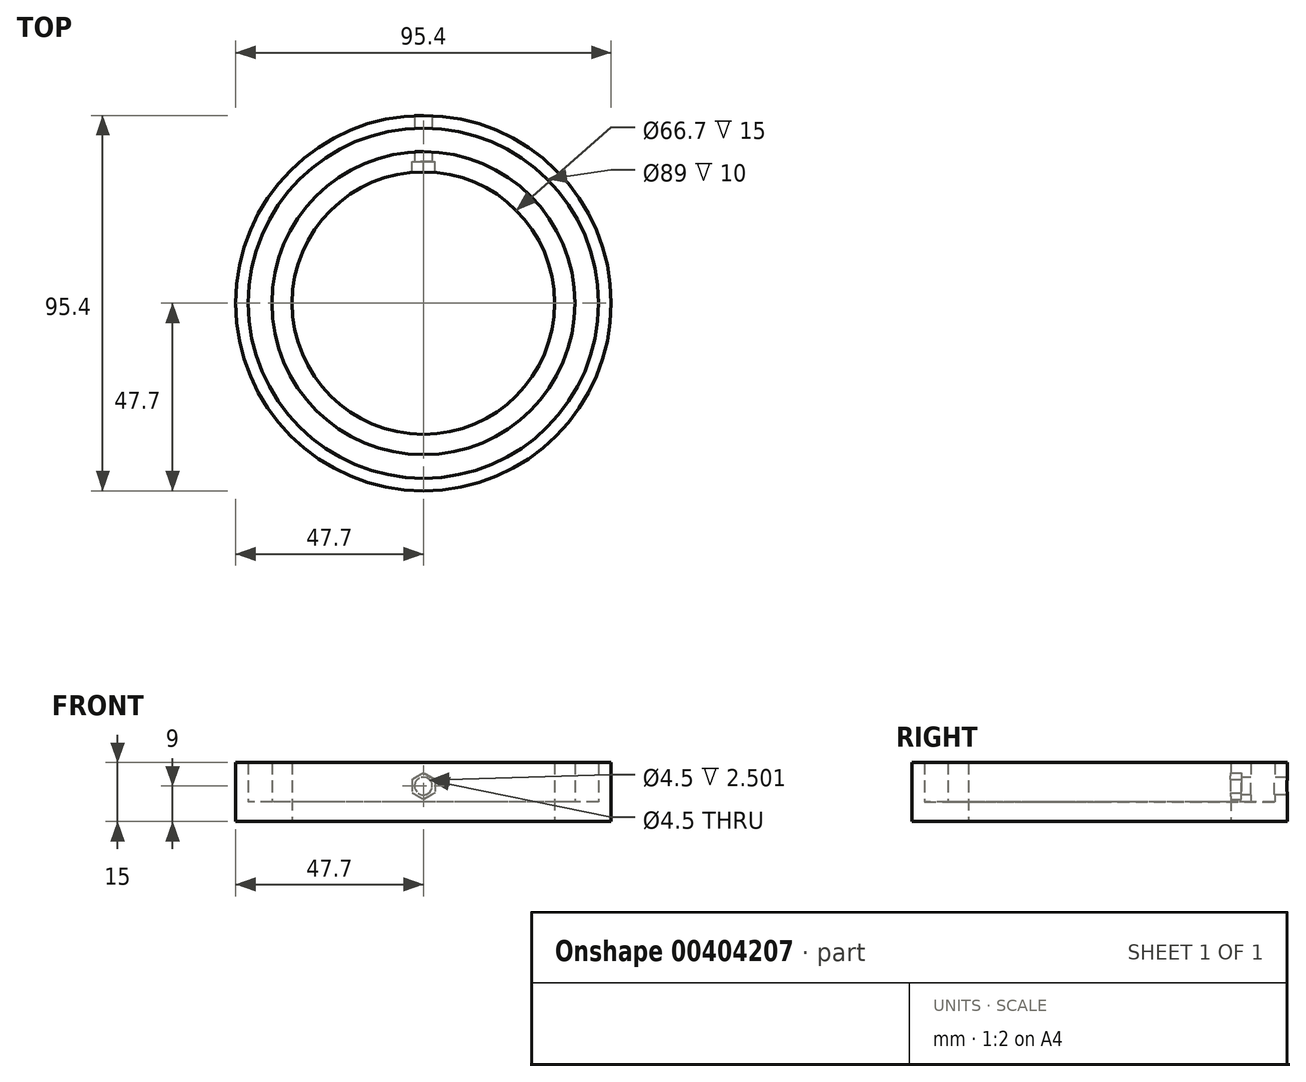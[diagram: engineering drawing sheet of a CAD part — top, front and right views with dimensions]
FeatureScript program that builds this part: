
annotation { "Feature Type Name" : "Feature", "Feature Type Description" : "" }
export const myFeature = defineFeature(function(context is Context, id is Id, definition is map)
    precondition{}
    {
        {
            var Q0;
            Q0=qCreatedBy(makeId("Top.planeOp"),FACE);
            var sketch = newSketch(context, id + "F0", { "sketchPlane" : qUnion([Q0])});
            skCircle(sketch, "E0", {"center": v(0, 0) * mm, "radius": 33.35 * mm});
            skCircle(sketch, "E1", {"center": v(0, 0) * mm, "radius": 38.5 * mm});
            skSolve(sketch);
        }
        {
            var Q0;
            Q0 = qSketchRegion(id + "F0", true);
            extrude(context, id + "F1", {"entities" : qUnion([Q0]), "depth" : 15 * mm});
        }
        {
            var Q0;
            Q0=qCreatedBy(makeId("Top.planeOp"),FACE);
            var sketch = newSketch(context, id + "F2", { "sketchPlane" : qUnion([Q0])});
            skCircle(sketch, "E2", {"center": v(0, 0) * mm, "radius": 44.5 * mm});
            skCircle(sketch, "E3", {"center": v(0, 0) * mm, "radius": 38.5 * mm});
            skSolve(sketch);
        }
        {
            var Q0;
            Q0 = qSketchRegion(id + "F2", true);
            extrude(context, id + "F3", {"entities" : qUnion([Q0]), "operationType" : NewBodyOperationType.ADD, "depth" : 5 * mm});
        }
        {
            var Q0;
            Q0=qCreatedBy(makeId("Top.planeOp"),FACE);
            var sketch = newSketch(context, id + "F4", { "sketchPlane" : qUnion([Q0])});
            skCircle(sketch, "E4", {"center": v(0, 0) * mm, "radius": 47.7 * mm});
            skCircle(sketch, "E5", {"center": v(0, 0) * mm, "radius": 44.5 * mm});
            skSolve(sketch);
        }
        {
            var Q0;
            Q0 = qSketchRegion(id + "F4", true);
            extrude(context, id + "F5", {"entities" : qUnion([Q0]), "operationType" : NewBodyOperationType.ADD, "depth" : 15 * mm});
        }
        {
            var Q0;
            Q0=qCreatedBy(makeId("Front.planeOp"),FACE);
            var sketch = newSketch(context, id + "F6", { "sketchPlane" : qUnion([Q0])});
            skCircle(sketch, "E6", {"center": v(0, 9) * mm, "radius": 2.25 * mm});
            skSolve(sketch);
        }
        {
            var Q0;
            Q0 = qSketchRegion(id + "F6", true);
            extrude(context, id + "F7", {"entities" : qUnion([Q0]), "operationType" : NewBodyOperationType.REMOVE, "endBound" : BoundingType.THROUGH_ALL, "oppositeDirection" : true, "depth" : 25 * mm});
        }
        {
            var Q0;
            Q0=qCreatedBy(makeId("Front.planeOp"),FACE);
            cPlane(context, id + "F8", {"entities" : qUnion([Q0]), "cplaneType" : CPlaneType.OFFSET, "offset" : 36 * mm, "oppositeDirection" : true, "width" : 150 * mm, "height" : 150 * mm});
        }
        {
            var Q0;
            Q0=qCreatedBy(id+"F8.planeOp",FACE);
            var sketch = newSketch(context, id + "F9", { "sketchPlane" : qUnion([Q0])});
            skCircle(sketch, "E7.cCircle", {"center": v(0, 9) * mm, "radius": 2.92 * mm, "construction": true});
            skLineSegment(sketch, "E7.0", {"start": v(2.92, 10.68) * mm, "end": v(2.92, 7.32) * mm});
            skLineSegment(sketch, "E7.1", {"start": v(2.92, 7.32) * mm, "end": v(0, 5.63) * mm});
            skLineSegment(sketch, "E7.2", {"start": v(0, 5.63) * mm, "end": v(-2.92, 7.32) * mm});
            skLineSegment(sketch, "E7.3", {"start": v(-2.92, 7.32) * mm, "end": v(-2.92, 10.68) * mm});
            skLineSegment(sketch, "E7.4", {"start": v(-2.92, 10.68) * mm, "end": v(0, 12.37) * mm});
            skLineSegment(sketch, "E7.5", {"start": v(0, 12.37) * mm, "end": v(2.92, 10.68) * mm});
            skPoint(sketch, "E7.0.midPoint", {"position": v(2.92, 9) * mm});
            skSolve(sketch);
        }
        {
            var Q0;
            Q0 = qSketchRegion(id + "F9", true);
            extrude(context, id + "F10", {"entities" : qUnion([Q0]), "operationType" : NewBodyOperationType.REMOVE, "depth" : 4 * mm});
        }
    });
